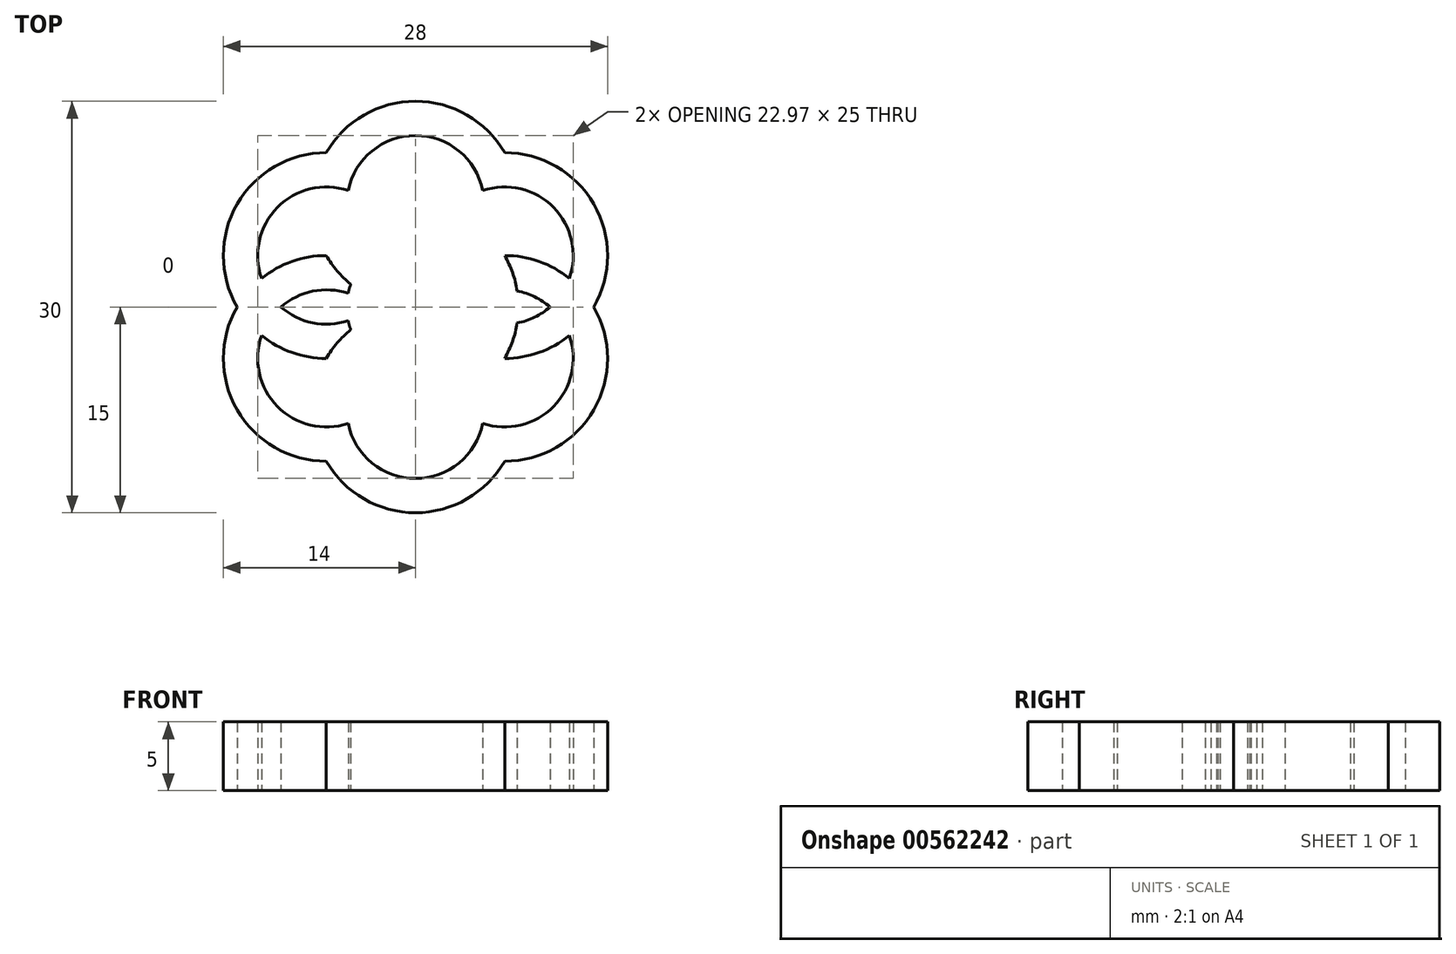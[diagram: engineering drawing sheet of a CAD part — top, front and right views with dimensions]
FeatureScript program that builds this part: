
annotation { "Feature Type Name" : "Feature", "Feature Type Description" : "" }
export const myFeature = defineFeature(function(context is Context, id is Id, definition is map)
    precondition{}
    {
        {
            var Q0;
            Q0=qCreatedBy(makeId("Top.planeOp"),FACE);
            var sketch = newSketch(context, id + "F0", { "sketchPlane" : qUnion([Q0])});
            skCircle(sketch, "E0", {"center": v(0, 0) * mm, "radius": 5 * mm});
            skCircle(sketch, "E1", {"center": v(0, 0) * mm, "radius": 7.5 * mm});
            skLineSegment(sketch, "E2", {"start": v(0, -7.5) * mm, "end": v(0, 7.5) * mm, "construction": true});
            skLineSegment(sketch, "E3", {"start": v(6.5, 3.75) * mm, "end": v(-6.5, -3.75) * mm, "construction": true});
            skLineSegment(sketch, "E4", {"start": v(-6.5, 3.75) * mm, "end": v(6.5, -3.75) * mm, "construction": true});
            skCircle(sketch, "E5", {"center": v(0, -7.5) * mm, "radius": 7.5 * mm});
            skCircle(sketch, "E6", {"center": v(0, -7.5) * mm, "radius": 5 * mm});
            skCircle(sketch, "E7", {"center": v(6.5, -3.75) * mm, "radius": 7.5 * mm});
            skCircle(sketch, "E8", {"center": v(6.5, 3.75) * mm, "radius": 7.5 * mm});
            skCircle(sketch, "E9", {"center": v(0, 7.5) * mm, "radius": 7.5 * mm});
            skCircle(sketch, "E10", {"center": v(-6.5, 3.75) * mm, "radius": 7.5 * mm});
            skCircle(sketch, "E11", {"center": v(-6.5, -3.75) * mm, "radius": 7.5 * mm});
            skCircle(sketch, "E12", {"center": v(0, 0) * mm, "radius": 2.5 * mm});
            skCircle(sketch, "E13", {"center": v(-6.5, -3.75) * mm, "radius": 5 * mm});
            skCircle(sketch, "E14", {"center": v(-6.5, 3.75) * mm, "radius": 5 * mm});
            skCircle(sketch, "E15", {"center": v(0, 7.5) * mm, "radius": 5 * mm});
            skCircle(sketch, "E16", {"center": v(6.5, 3.75) * mm, "radius": 5 * mm});
            skCircle(sketch, "E17", {"center": v(6.5, -3.75) * mm, "radius": 5 * mm});
            skSolve(sketch);
        }
        {
            var Q0;
            Q0 = qSketchRegion(id + "F0", true);
            var Q1;
            {var subQ3=sQuery(id+"F0.wireOp",EDGE,"E10");var subQ5=sQuery(id+"F0.wireOp",EDGE,"E13");var subQ6=makeQuery(id+"F0.imprint","INTERSECT",VERTEX,{"disambiguationData":[OD(0.0)],"derivedFrom":[subQ3,subQ5]});Q1=makeQuery(id+"F0.imprint","IMPRINT",FACE,{"disambiguationData":[TD([[makeQuery(id+"F0.imprint","IMPRINT",EDGE,{"disambiguationData":[TD([[subQ6,1.0]])],"derivedFrom":subQ5}),1.0]])]});}
            var Q2;
            {var subQ0=sQuery(id+"F0.wireOp",EDGE,"E13");var subQ1=sQuery(id+"F0.wireOp",EDGE,"E1");var subQ2=makeQuery(id+"F0.imprint","INTERSECT",VERTEX,{"disambiguationData":[OD(0.0)],"derivedFrom":[subQ1,subQ0]});Q2=makeQuery(id+"F0.imprint","IMPRINT",FACE,{"disambiguationData":[TD([[makeQuery(id+"F0.imprint","IMPRINT",EDGE,{"disambiguationData":[TD([[subQ2,-1.0]])],"derivedFrom":subQ0}),-1.0]])]});}
            var Q3;
            {var subQ0=sQuery(id+"F0.wireOp",EDGE,"E9");var subQ1=sQuery(id+"F0.wireOp",EDGE,"E0");var subQ2=makeQuery(id+"F0.imprint","INTERSECT",VERTEX,{"disambiguationData":[OD(1.0)],"derivedFrom":[subQ1,subQ0]});Q3=makeQuery(id+"F0.imprint","IMPRINT",FACE,{"disambiguationData":[TD([[makeQuery(id+"F0.imprint","IMPRINT",EDGE,{"disambiguationData":[TD([[subQ2,-1.0]])],"derivedFrom":subQ1}),-1.0]])]});}
            var Q4;
            {var subQ0=sQuery(id+"F0.wireOp",EDGE,"E14");var subQ1=sQuery(id+"F0.wireOp",EDGE,"E0");var subQ2=makeQuery(id+"F0.imprint","INTERSECT",VERTEX,{"disambiguationData":[OD(1.0)],"derivedFrom":[subQ1,subQ0]});Q4=makeQuery(id+"F0.imprint","IMPRINT",FACE,{"disambiguationData":[TD([[makeQuery(id+"F0.imprint","IMPRINT",EDGE,{"disambiguationData":[TD([[subQ2,-1.0]])],"derivedFrom":subQ1}),-1.0]])]});}
            var Q5;
            {var subQ0=sQuery(id+"F0.wireOp",EDGE,"E16");var subQ1=sQuery(id+"F0.wireOp",EDGE,"E1");var subQ2=makeQuery(id+"F0.imprint","INTERSECT",VERTEX,{"disambiguationData":[OD(1.0)],"derivedFrom":[subQ1,subQ0]});Q5=makeQuery(id+"F0.imprint","IMPRINT",FACE,{"disambiguationData":[TD([[makeQuery(id+"F0.imprint","IMPRINT",EDGE,{"disambiguationData":[TD([[subQ2,-1.0]])],"derivedFrom":subQ0}),-1.0]])]});}
            var Q6;
            {var subQ3=sQuery(id+"F0.wireOp",EDGE,"E7");var subQ5=sQuery(id+"F0.wireOp",EDGE,"E16");var subQ6=makeQuery(id+"F0.imprint","INTERSECT",VERTEX,{"disambiguationData":[OD(0.0)],"derivedFrom":[subQ3,subQ5]});Q6=makeQuery(id+"F0.imprint","IMPRINT",FACE,{"disambiguationData":[TD([[makeQuery(id+"F0.imprint","IMPRINT",EDGE,{"disambiguationData":[TD([[subQ6,1.0]])],"derivedFrom":subQ5}),1.0]])]});}
            extrude(context, id + "F1", {"entities" : qUnion([Q0, Q1, Q2, Q3, Q4, Q5, Q6]), "depth" : 5 * mm, "offsetDistance" : 25 * mm});
        }
    });
